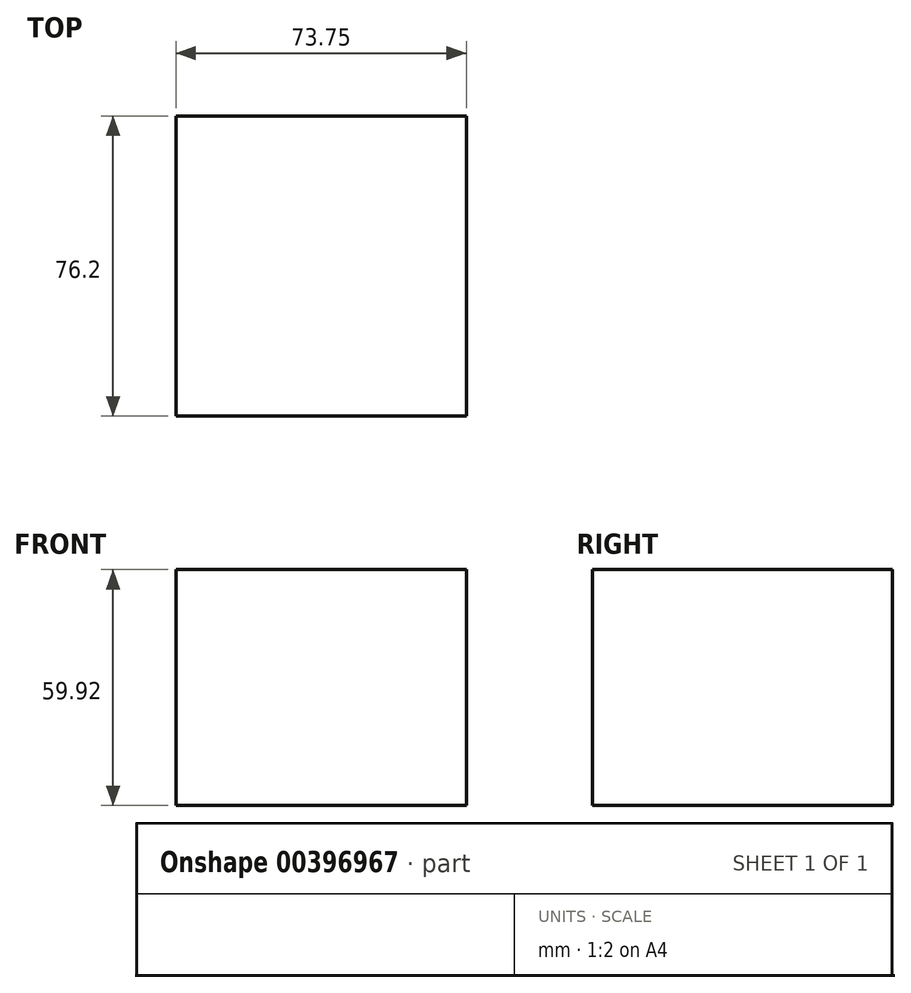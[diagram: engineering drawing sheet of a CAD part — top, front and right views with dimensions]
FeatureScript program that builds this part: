
annotation { "Feature Type Name" : "Feature", "Feature Type Description" : "" }
export const myFeature = defineFeature(function(context is Context, id is Id, definition is map)
    precondition{}
    {
        {
            var Q0;
            Q0=qCreatedBy(makeId("Front.planeOp"),FACE);
            var sketch = newSketch(context, id + "F0", { "sketchPlane" : qUnion([Q0])});
            skLineSegment(sketch, "E0.bottom", {"start": v(-37.35, 30.15) * mm, "end": v(36.4, 30.15) * mm});
            skLineSegment(sketch, "E0.top", {"start": v(-37.35, -29.77) * mm, "end": v(36.4, -29.77) * mm});
            skLineSegment(sketch, "E0.left", {"start": v(-37.35, 30.15) * mm, "end": v(-37.35, -29.77) * mm});
            skLineSegment(sketch, "E0.right", {"start": v(36.4, 30.15) * mm, "end": v(36.4, -29.77) * mm});
            skSolve(sketch);
        }
        {
            var Q0;
            Q0 = qSketchRegion(id + "F0", true);
            extrude(context, id + "F1", {"entities" : qUnion([Q0]), "depth" : 76.2 * mm});
        }
    });
